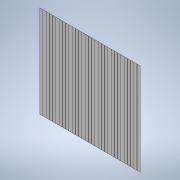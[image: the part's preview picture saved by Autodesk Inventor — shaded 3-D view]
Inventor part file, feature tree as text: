
AUTODESK INVENTOR PART (.ipt)
format: ipt  version: 2021 (Build 250183000, 183)  size: 222,208 bytes
history: native  units: in
note: dims shown in document units (in); Inventor stores cm internally (conversion verified against a paired STEP export)
features: extrude x3, sketch x3, pattern_linear x1, projected_geometry x1
ambient origin geometry x8: Origin, YZ Plane, XZ Plane, XY Plane, X Axis, Y Axis, Z Axis, Center Point
bodies: Solid1 (feature_tree)
feature tree (8):
  extrude  "Extrusion1"  Depth=3.0in
  extrude  "Extrusion2"  Depth=0.1in
  pattern_linear  "Rectangular Pattern1"  Count1=31 Spacing1=0.106in
  extrude  "Extrusion3"  Depth=0.106in TaperAngle=0.0deg
  sketch  "Sketch1"  dims[d0=4.0in d1=3.0in]
  sketch  "Sketch2"  dims[d2=0.04in d3=0.0in d4=0.1in]
  projected_geometry  "Projected Loop1"
  sketch  "Sketch3"  dims[d5=0.0015in d6=0.0in d7=12.2047in d9=0.106in d10=1.0in d11=0.0in]
